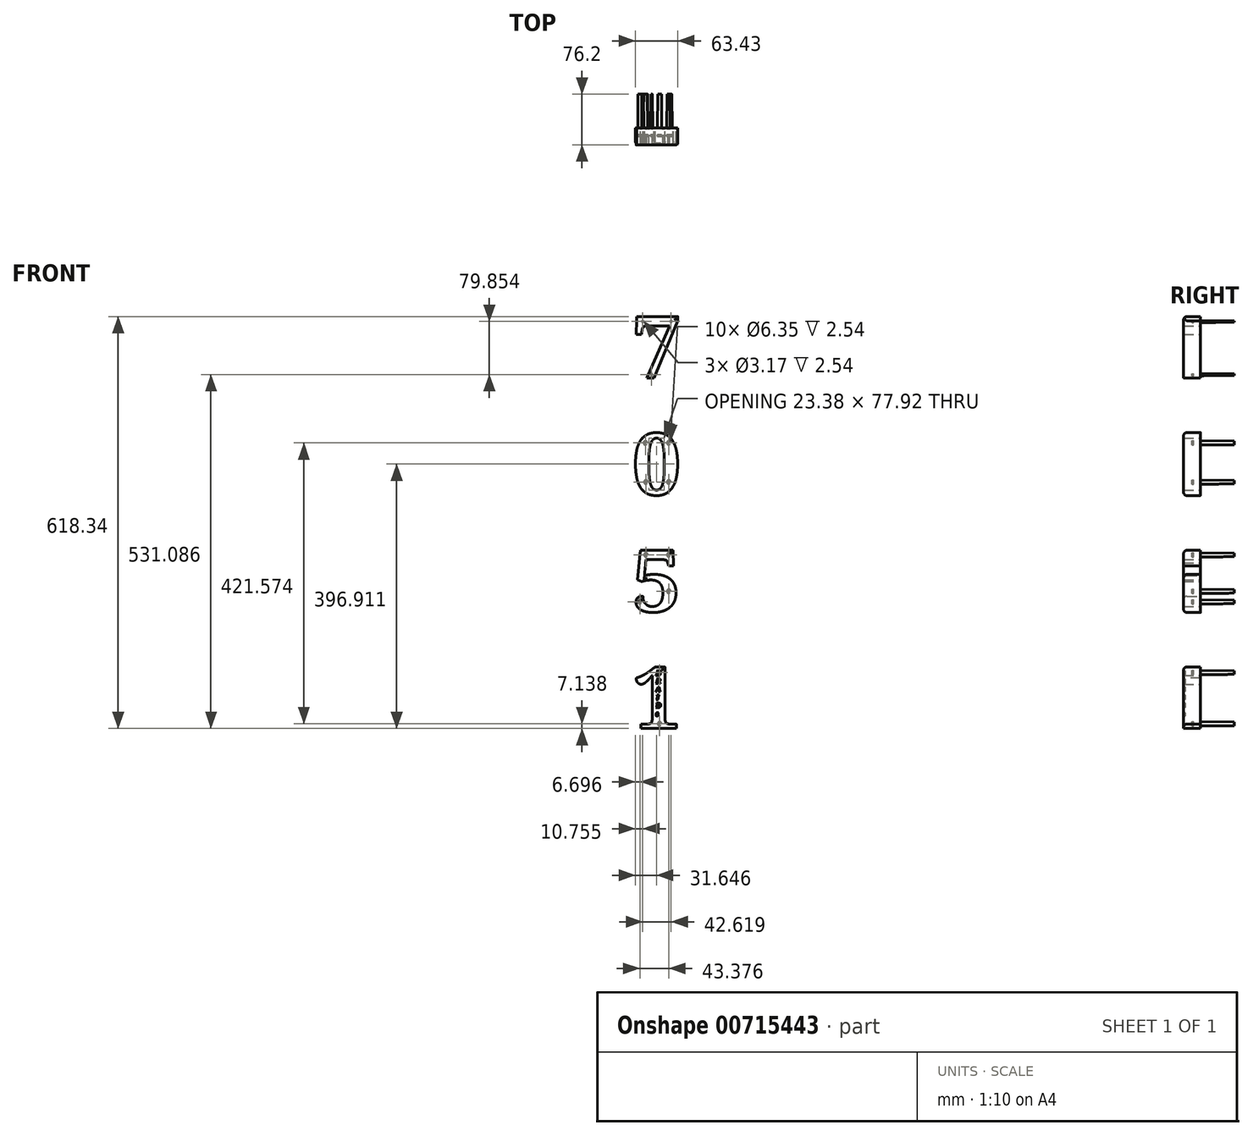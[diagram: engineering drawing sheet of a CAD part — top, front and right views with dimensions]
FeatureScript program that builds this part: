
annotation { "Feature Type Name" : "Feature", "Feature Type Description" : "" }
export const myFeature = defineFeature(function(context is Context, id is Id, definition is map)
    precondition{}
    {
        {
            var Q0;
            Q0=qCreatedBy(makeId("Front.planeOp"),FACE);
            var sketch = newSketch(context, id + "F0", { "sketchPlane" : qUnion([Q0])});
            skText(sketch, "E0", { "text": "7\n0\n5\n1", "fontName": "NotoSerif-Bold.ttf"});
            const initialGuessF0  = {"E0": [-0.0381, 0, 1, 0, 0.09287]};
            skSetInitialGuess(sketch, initialGuessF0);
            skSolve(sketch);
        }
        {
            var Q0;
            Q0 = qSketchRegion(id + "F0", true);
            extrude(context, id + "F1", {"entities" : qUnion([Q0]), "depth" : 25.4 * mm, "offsetDistance" : 25.4 * mm});
        }
        {
            var Q0;
            Q0=makeQuery(id+"F1.opExtrude","CAP_EDGE",EDGE,{"disambiguationData":[OSD([sQuery(id+"F0.wireOp",EDGE,"E0.sketch_text.stroke-9")])],"isStart":false});
            var Q1;
            Q1=makeQuery(id+"F1.opExtrude","CAP_EDGE",EDGE,{"disambiguationData":[OSD([sQuery(id+"F0.wireOp",EDGE,"E0.sketch_text.stroke-7")])],"isStart":false});
            var Q2;
            Q2=makeQuery(id+"F1.opExtrude","CAP_EDGE",EDGE,{"disambiguationData":[OSD([sQuery(id+"F0.wireOp",EDGE,"E0.sketch_text.stroke-23")])],"isStart":false});
            var Q3;
            Q3=makeQuery(id+"F1.opExtrude","CAP_EDGE",EDGE,{"disambiguationData":[OSD([sQuery(id+"F0.wireOp",EDGE,"E0.sketch_text.stroke-55")])],"isStart":false});
            var Q4;
            Q4=makeQuery(id+"F1.opExtrude","CAP_EDGE",EDGE,{"disambiguationData":[OSD([sQuery(id+"F0.wireOp",EDGE,"E0.sketch_text.stroke-56")])],"isStart":false});
            var Q5;
            Q5=makeQuery(id+"F1.opExtrude","CAP_EDGE",EDGE,{"disambiguationData":[OSD([sQuery(id+"F0.wireOp",EDGE,"E0.sketch_text.stroke-73")])],"isStart":false});
            var Q6;
            Q6=makeQuery(id+"F1.opExtrude","CAP_EDGE",EDGE,{"disambiguationData":[OSD([sQuery(id+"F0.wireOp",EDGE,"E0.sketch_text.stroke-111")])],"isStart":false});
            var Q7;
            Q7=makeQuery(id+"F1.opExtrude","CAP_EDGE",EDGE,{"disambiguationData":[OSD([sQuery(id+"F0.wireOp",EDGE,"E0.sketch_text.stroke-112")])],"isStart":false});
            fillet(context, id + "F2", {"entities" : qUnion([Q0, Q1, Q2, Q3, Q4, Q5, Q6, Q7]), "radius" : 5.08 * mm, "tangentPropagation" : true, "allowEdgeOverflow" : false});
        }
        {
            var Q0;
            Q0=makeQuery(id+"F0.imprint","IMPRINT",FACE,{"disambiguationData":[TD([[makeQuery(id+"F0.imprint","IMPRINT",EDGE,{"derivedFrom":sQuery(id+"F0.wireOp",EDGE,"E0.sketch_text.stroke-0")}),-1.0]])]});
            var sketch = newSketch(context, id + "F3", { "sketchPlane" : qUnion([Q0])});
            skCircle(sketch, "E1", {"center": v(19.68, 84.68) * mm, "radius": 1.59 * mm});
            skCircle(sketch, "E2", {"center": v(-22.93, 84.68) * mm, "radius": 1.59 * mm});
            skCircle(sketch, "E3", {"center": v(-9.42, 4.83) * mm, "radius": 1.59 * mm});
            skCircle(sketch, "E4", {"center": v(-18.64, -97.55) * mm, "radius": 3.18 * mm});
            skCircle(sketch, "E5", {"center": v(-17.95, -156.34) * mm, "radius": 3.18 * mm});
            skCircle(sketch, "E6", {"center": v(16.38, -97.55) * mm, "radius": 3.18 * mm});
            skCircle(sketch, "E7", {"center": v(16.38, -156.34) * mm, "radius": 3.18 * mm});
            skCircle(sketch, "E8", {"center": v(16.38, -265.61) * mm, "radius": 3.18 * mm});
            skCircle(sketch, "E9", {"center": v(-17.95, -265.61) * mm, "radius": 3.18 * mm});
            skCircle(sketch, "E10", {"center": v(16.38, -320.3) * mm, "radius": 3.18 * mm});
            skCircle(sketch, "E11", {"center": v(-27, -336.1) * mm, "radius": 3.18 * mm});
            skCircle(sketch, "E12", {"center": v(2.54, -519.12) * mm, "radius": 3.18 * mm});
            skCircle(sketch, "E13", {"center": v(2.54, -442.2) * mm, "radius": 3.18 * mm});
            skSolve(sketch);
        }
        {
            var Q0;
            Q0 = qSketchRegion(id + "F3", true);
            var Q1;
            Q1=sQuery(id+"F3.wireOp",EDGE,"E13");
            var Q2;
            Q2=sQuery(id+"F3.wireOp",EDGE,"E12");
            var Q3;
            Q3=sQuery(id+"F3.wireOp",EDGE,"E8");
            var Q4;
            Q4=sQuery(id+"F3.wireOp",EDGE,"E9");
            var Q5;
            Q5=sQuery(id+"F3.wireOp",EDGE,"E10");
            var Q6;
            Q6=sQuery(id+"F3.wireOp",EDGE,"E11");
            var Q7;
            Q7=sQuery(id+"F3.wireOp",EDGE,"E6");
            var Q8;
            Q8=sQuery(id+"F3.wireOp",EDGE,"E7");
            var Q9;
            Q9=sQuery(id+"F3.wireOp",EDGE,"E5");
            var Q10;
            Q10=sQuery(id+"F3.wireOp",EDGE,"E4");
            var Q11;
            Q11=sQuery(id+"F3.wireOp",EDGE,"E3");
            var Q12;
            Q12=sQuery(id+"F3.wireOp",EDGE,"E1");
            var Q13;
            Q13=sQuery(id+"F3.wireOp",EDGE,"E2");
            extrude(context, id + "F4", {"entities" : qUnion([Q0]), "operationType" : NewBodyOperationType.ADD, "surfaceOperationType" : NewSurfaceOperationType.ADD, "surfaceEntities" : qUnion([Q1, Q2, Q3, Q4, Q5, Q6, Q7, Q8, Q9, Q10, Q11, Q12, Q13]), "oppositeDirection" : true, "depth" : 50.8 * mm, "offsetDistance" : 25.4 * mm, "hasDraft" : true, "draftAngle" : .5 * degree, "draftPullDirection" : true});
        }
        {
            var Q0;
            Q0=makeQuery(id+"F1.opExtrude","CAP_FACE",FACE,{"disambiguationData":[OSD([sQuery(id+"F0.wireOp",EDGE,"E0.sketch_text.stroke-91"),sQuery(id+"F0.wireOp",EDGE,"E0.sketch_text.stroke-92"),sQuery(id+"F0.wireOp",EDGE,"E0.sketch_text.stroke-93"),sQuery(id+"F0.wireOp",EDGE,"E0.sketch_text.stroke-94"),sQuery(id+"F0.wireOp",EDGE,"E0.sketch_text.stroke-95"),sQuery(id+"F0.wireOp",EDGE,"E0.sketch_text.stroke-96"),sQuery(id+"F0.wireOp",EDGE,"E0.sketch_text.stroke-97"),sQuery(id+"F0.wireOp",EDGE,"E0.sketch_text.stroke-98"),sQuery(id+"F0.wireOp",EDGE,"E0.sketch_text.stroke-99"),sQuery(id+"F0.wireOp",EDGE,"E0.sketch_text.stroke-100"),sQuery(id+"F0.wireOp",EDGE,"E0.sketch_text.stroke-101"),sQuery(id+"F0.wireOp",EDGE,"E0.sketch_text.stroke-102"),sQuery(id+"F0.wireOp",EDGE,"E0.sketch_text.stroke-103"),sQuery(id+"F0.wireOp",EDGE,"E0.sketch_text.stroke-104"),sQuery(id+"F0.wireOp",EDGE,"E0.sketch_text.stroke-105"),sQuery(id+"F0.wireOp",EDGE,"E0.sketch_text.stroke-106"),sQuery(id+"F0.wireOp",EDGE,"E0.sketch_text.stroke-107"),sQuery(id+"F0.wireOp",EDGE,"E0.sketch_text.stroke-108"),sQuery(id+"F0.wireOp",EDGE,"E0.sketch_text.stroke-109"),sQuery(id+"F0.wireOp",EDGE,"E0.sketch_text.stroke-110"),sQuery(id+"F0.wireOp",EDGE,"E0.sketch_text.stroke-111"),sQuery(id+"F0.wireOp",EDGE,"E0.sketch_text.stroke-112"),sQuery(id+"F0.wireOp",EDGE,"E0.sketch_text.stroke-113"),sQuery(id+"F0.wireOp",EDGE,"E0.sketch_text.stroke-114"),sQuery(id+"F0.wireOp",EDGE,"E0.sketch_text.stroke-115"),sQuery(id+"F0.wireOp",EDGE,"E0.sketch_text.stroke-116"),sQuery(id+"F0.wireOp",EDGE,"E0.sketch_text.stroke-117"),sQuery(id+"F0.wireOp",EDGE,"E0.sketch_text.stroke-118"),sQuery(id+"F0.wireOp",EDGE,"E0.sketch_text.stroke-119")])],"isStart":false});
            var sketch = newSketch(context, id + "F5", { "sketchPlane" : qUnion([Q0])});
            skText(sketch, "E14", { "text": "B\nR \nA\n\nD\ns", "fontName": "Tinos-BoldItalic.ttf"});
            skText(sketch, "E15", { "text": "B\nR \nA\n\nD\ns", "fontName": "Tinos-BoldItalic.ttf"});
            skText(sketch, "E16", { "text": "I", "fontName": "Tinos-BoldItalic.ttf"});
            skPoint(sketch, "E16.firstSnap0", {"position": v(-8.56, -478.7) * mm});
            const initialGuessF5  = {"E14": [-0.00303, -0.44636, 1, 0, 0.00762], "E15": [-0.03593, -0.89342, 1, 0, 0.00762], "E16": [-0.0026, -0.48302, 1, 0, 0.00762]};
            skSetInitialGuess(sketch, initialGuessF5);
            skSolve(sketch);
        }
        {
            var Q0;
            Q0 = qSketchRegion(id + "F5", true);
            extrude(context, id + "F6", {"entities" : qUnion([Q0]), "operationType" : NewBodyOperationType.REMOVE, "oppositeDirection" : true, "depth" : 2.54 * mm, "offsetDistance" : 25.4 * mm});
        }
        {
            var Q0;
            Q0 = qSketchRegion(id + "F3", true);
            extrude(context, id + "F7", {"entities" : qUnion([Q0]), "operationType" : NewBodyOperationType.REMOVE, "depth" : 12.7 * mm, "offsetDistance" : 25.4 * mm});
        }
        {
            var Q0;
            Q0 = qSketchRegion(id + "F3", true);
            extrude(context, id + "F8", {"entities" : qUnion([Q0]), "operationType" : NewBodyOperationType.ADD, "depth" : 10.16 * mm, "offsetDistance" : 25.4 * mm});
        }
    });
